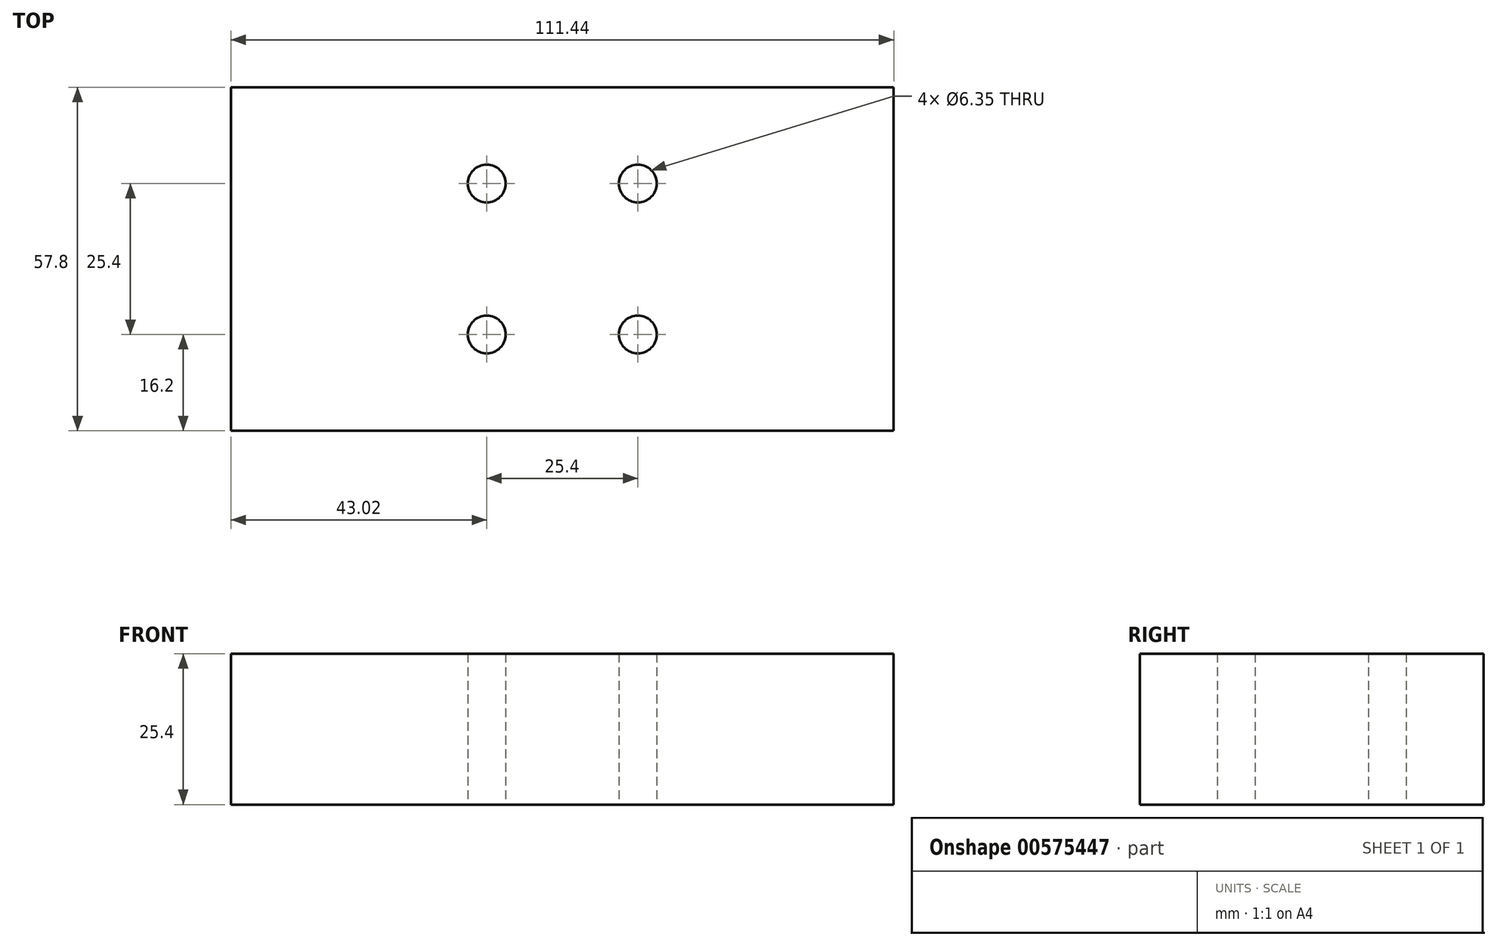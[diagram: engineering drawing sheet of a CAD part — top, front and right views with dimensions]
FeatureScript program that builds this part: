
annotation { "Feature Type Name" : "Feature", "Feature Type Description" : "" }
export const myFeature = defineFeature(function(context is Context, id is Id, definition is map)
    precondition{}
    {
        {
            var Q0;
            Q0=qCreatedBy(makeId("Top.planeOp"),FACE);
            var sketch = newSketch(context, id + "F0", { "sketchPlane" : qUnion([Q0])});
            skLineSegment(sketch, "E0.bottom", {"start": v(55.72, 28.9) * mm, "end": v(-55.72, 28.9) * mm});
            skLineSegment(sketch, "E0.top", {"start": v(55.72, -28.9) * mm, "end": v(-55.72, -28.9) * mm});
            skLineSegment(sketch, "E0.left", {"start": v(55.72, 28.9) * mm, "end": v(55.72, -28.9) * mm});
            skLineSegment(sketch, "E0.right", {"start": v(-55.72, 28.9) * mm, "end": v(-55.72, -28.9) * mm});
            skPoint(sketch, "E0.middle", {"position": v(0, 0) * mm});
            skSolve(sketch);
        }
        {
            var Q0;
            Q0=makeQuery(id+"F0.imprint","IMPRINT",FACE,{"disambiguationData":[TD([[makeQuery(id+"F0.imprint","IMPRINT",EDGE,{"derivedFrom":sQuery(id+"F0.wireOp",EDGE,"E0.bottom")}),1.0]])]});
            var sketch = newSketch(context, id + "F1", { "sketchPlane" : qUnion([Q0])});
            skSolve(sketch);
        }
        {
            var Q0;
            Q0=makeQuery(id+"F1.imprint","IMPRINT",FACE,{"disambiguationData":[TD([[makeQuery(id+"F1.imprint","IMPRINT",EDGE,{"derivedFrom":makeQuery(id+"F0.imprint","IMPRINT",EDGE,{"derivedFrom":sQuery(id+"F0.wireOp",EDGE,"E0.bottom")})}),1.0]])]});
            extrude(context, id + "F2", {"entities" : qUnion([Q0]), "depth" : 25.4 * mm, "offsetDistance" : 25.4 * mm});
        }
        {
            var Q0;
            Q0=qCreatedBy(makeId("Top.planeOp"),FACE);
            var sketch = newSketch(context, id + "F3", { "sketchPlane" : qUnion([Q0])});
            skLineSegment(sketch, "E1.bottom", {"start": v(12.7, 12.7) * mm, "end": v(-12.7, 12.7) * mm});
            skLineSegment(sketch, "E1.top", {"start": v(12.7, -12.7) * mm, "end": v(-12.7, -12.7) * mm});
            skLineSegment(sketch, "E1.left", {"start": v(12.7, 12.7) * mm, "end": v(12.7, -12.7) * mm});
            skLineSegment(sketch, "E1.right", {"start": v(-12.7, 12.7) * mm, "end": v(-12.7, -12.7) * mm});
            skPoint(sketch, "E1.middle", {"position": v(0, 0) * mm});
            skSolve(sketch);
        }
        {
            var Q0;
            Q0=sQuery(id+"F3.wireOp",VERTEX,"E1.top.start");
            var Q1;
            Q1=sQuery(id+"F3.wireOp",VERTEX,"E1.top.end");
            var Q2;
            Q2=sQuery(id+"F3.wireOp",VERTEX,"E1.bottom.end");
            var Q3;
            Q3=sQuery(id+"F3.wireOp",VERTEX,"E1.left.start");
            var Q4;
            Q4=makeQuery(id+"F2.opExtrude","SWEPT_BODY",BODY,{"disambiguationData":[OSD([sQuery(id+"F0.wireOp",EDGE,"E0.bottom"),sQuery(id+"F0.wireOp",EDGE,"E0.top"),sQuery(id+"F0.wireOp",EDGE,"E0.left"),sQuery(id+"F0.wireOp",EDGE,"E0.right")])]});
            hole(context, id + "F4", {"style" : HoleStyle.SIMPLE, "endStyle" : HoleEndStyle.THROUGH, "oppositeDirection" : true, "holeDiameter" : 6.35 * mm, "isTappedThrough" : true, "tappedDepth" : 12.7 * mm, "tapClearance" : 3, "locations" : qUnion([Q0, Q1, Q2, Q3]), "scope" : qUnion([Q4])});
        }
    });
